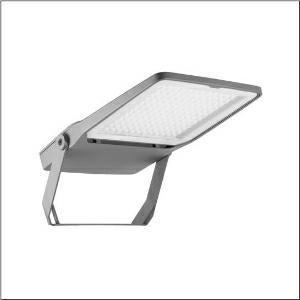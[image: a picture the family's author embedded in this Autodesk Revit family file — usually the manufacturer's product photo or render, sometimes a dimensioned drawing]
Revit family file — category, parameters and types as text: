
# Revit family: floodlight_fl_20_midi___pl52_5xa7682d3d1ac_4da3
name_source: partatom
category: Lighting Fixtures
units: mm (PartAtom-declared; Revit-internal decimal feet)

## family parameters
Cut with Voids When Loaded = No
Host = Face
Light Source = No
Part Type = Normal
Room Calculation Point = No
Round Connector Dimension = Use Diameter
Shared = No

## types (1)
- --- (1 x LED 5000K / CRI = 70 (unbekannt), 18250 lm, 5000K)
    Apparent Load = 142 VA
    CIE Flux Codes = 27 59 98 100 100
    Color Rendering = 70
    Color Temperature = 5000K
    Default Elevation = 1800 mm
    Description = Floodlight FL 20 midi, floodlight, primary light control with lens, of plastic, primary optical cover: protective disc, of toughened safety glass, transparent, light distribution: PL52, light emission: direct distribution, primary light characteristic: asymmetric, installation type: surface-mounted, LED High Power LED, rated luminous flux: 18.250 lm, light colour: 750, colour temperature: 5000K, control gear: ECG Plus, control: flexible luminous flux parameterisation, time-dependent luminous flux control, digital communication interface, power reduction, overheat protection, electronic power reduction, with terminal, 5-pole, max. 2.5mm², mains connection: 220..240V, AC, 50/60Hz, rated input power: 142W, LED unit, of diecast aluminium, powder-coated, Siteco® metallic grey (DB 702S), length: 654 mm, width: 450 mm, height: 76mm, housing frame, of diecast aluminium, powder-coated, Siteco® metallic grey (DB 702S), mounting bracket, of steel, powder-coated, Siteco® metallic grey (DB 702S), DALIprotection rating (complete): IP66, insulation class (complete): insulation class II (safety insulation), certification: CE, ENEC, VDE, protection symbol: D, permissible ambient temperature for indoor applications: -40..+40°C, permissible ambient temperature for outdoor applications: -40..+50°C, standard: DIN EN 12944, packaging unit: 1 piece

Light Distribution: PL52
    Height = 76 mm
    Lamp = 1 x LED 5000K / CRI >= 70 (unbekannt)
    Lamp Light Flux = 18250 lm
    Lamp count = 1
    Length = 672 mm
    Luminous efficacy = 129 lm/W
    Manufacturer = Siteco
    ModVariant = No
    Model = 5XA7682D3D1AC
    Number of Poles = 1
    OnlyDefault = Yes
    Power Factor = 1
    Product Name = Floodlight FL 20 midi | PL52
    Product group = floodlight | pylon top
    ProductGroupID = 6101
    Protection Class = Protection class II
    Protection Degree = IP 66
    RLX_Detail_Level = 1
    RlxData = <blob elided: 97617 chars, md5=6e4b80a3>
    Socket = socket
    Standby Power = 0 W
    System Light Flux = 18250 lm
    System Power = 142 W
    Type Comments = factory setting: luminous flux: 100 % | dim-lin: 254 | 489 mA
    Type Image = l_1005943.jpg
    URL = http://relux.com
    VarID = @adj_143187
    Voltage = 0 V
    Weight = 0.00 kg
    Width = 450 mm

## geometry (parser evidence)
native form markers: Blend x4, Sweep x10
no freeform markers — native parametric forms only
